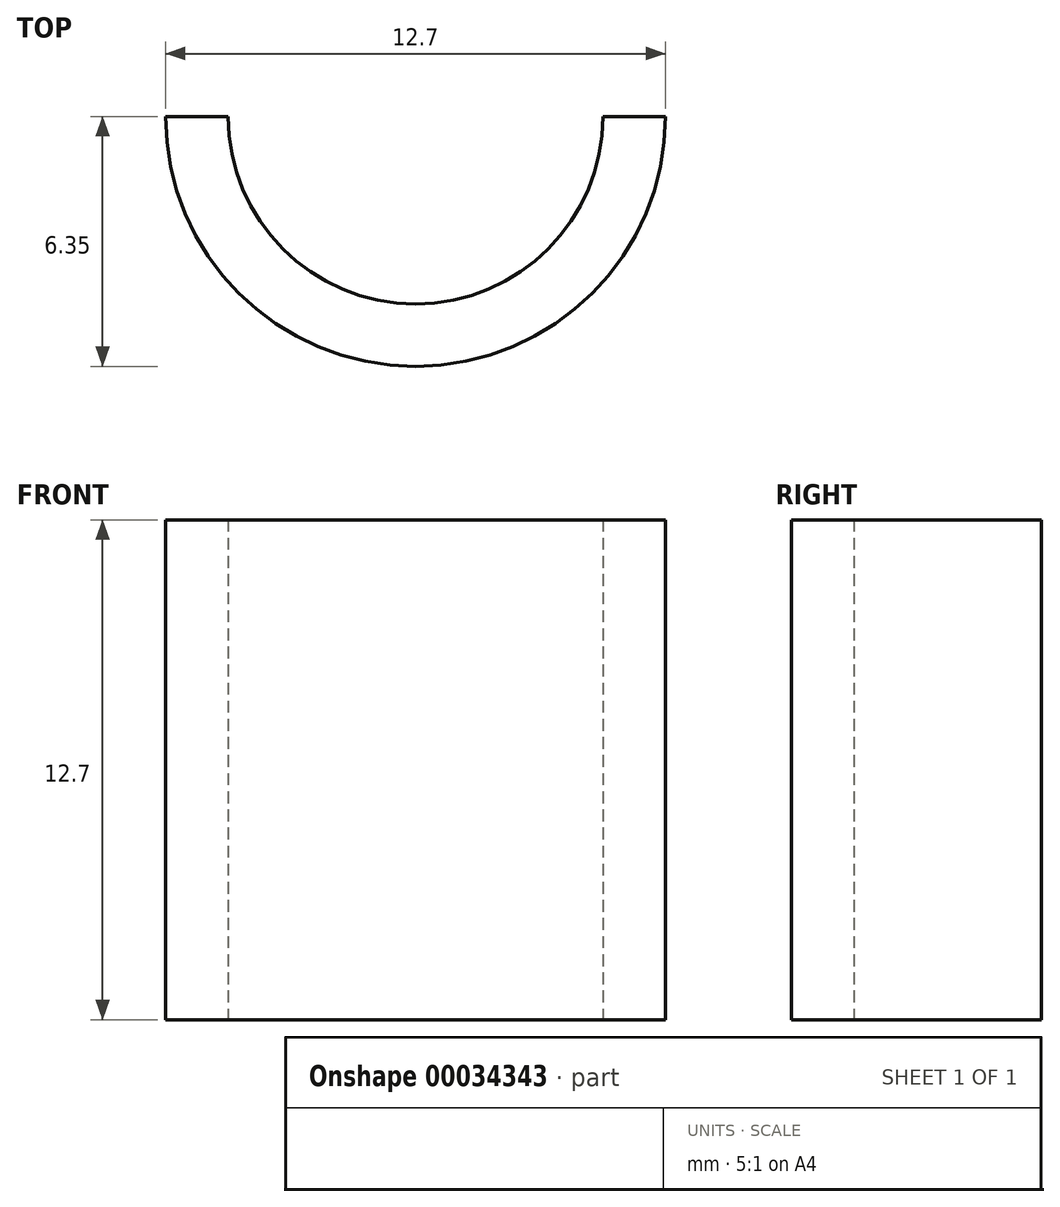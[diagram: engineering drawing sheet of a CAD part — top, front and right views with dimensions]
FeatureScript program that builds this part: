
annotation { "Feature Type Name" : "Feature", "Feature Type Description" : "" }
export const myFeature = defineFeature(function(context is Context, id is Id, definition is map)
    precondition{}
    {
        {
            var Q0;
            Q0=qCreatedBy(makeId("Top.planeOp"),FACE);
            var sketch = newSketch(context, id + "F0", { "sketchPlane" : qUnion([Q0])});
            skArc(sketch, "E0", {"start": v(-6.35, 0) * mm, "mid": v(0, -6.35) * mm, "end": v(6.35, 0) * mm});
            skArc(sketch, "E1", {"start": v(-4.76, 0) * mm, "mid": v(0, -4.76) * mm, "end": v(4.76, 0) * mm});
            skLineSegment(sketch, "E2", {"start": v(-6.35, 0) * mm, "end": v(-4.76, 0) * mm});
            skLineSegment(sketch, "E3.trimOffspring", {"start": v(4.76, 0) * mm, "end": v(6.35, 0) * mm});
            skSolve(sketch);
        }
        {
            var Q0;
            Q0 = qSketchRegion(id + "F0", true);
            extrude(context, id + "F1", {"entities" : qUnion([Q0]), "depth" : 12.7 * mm});
        }
    });
